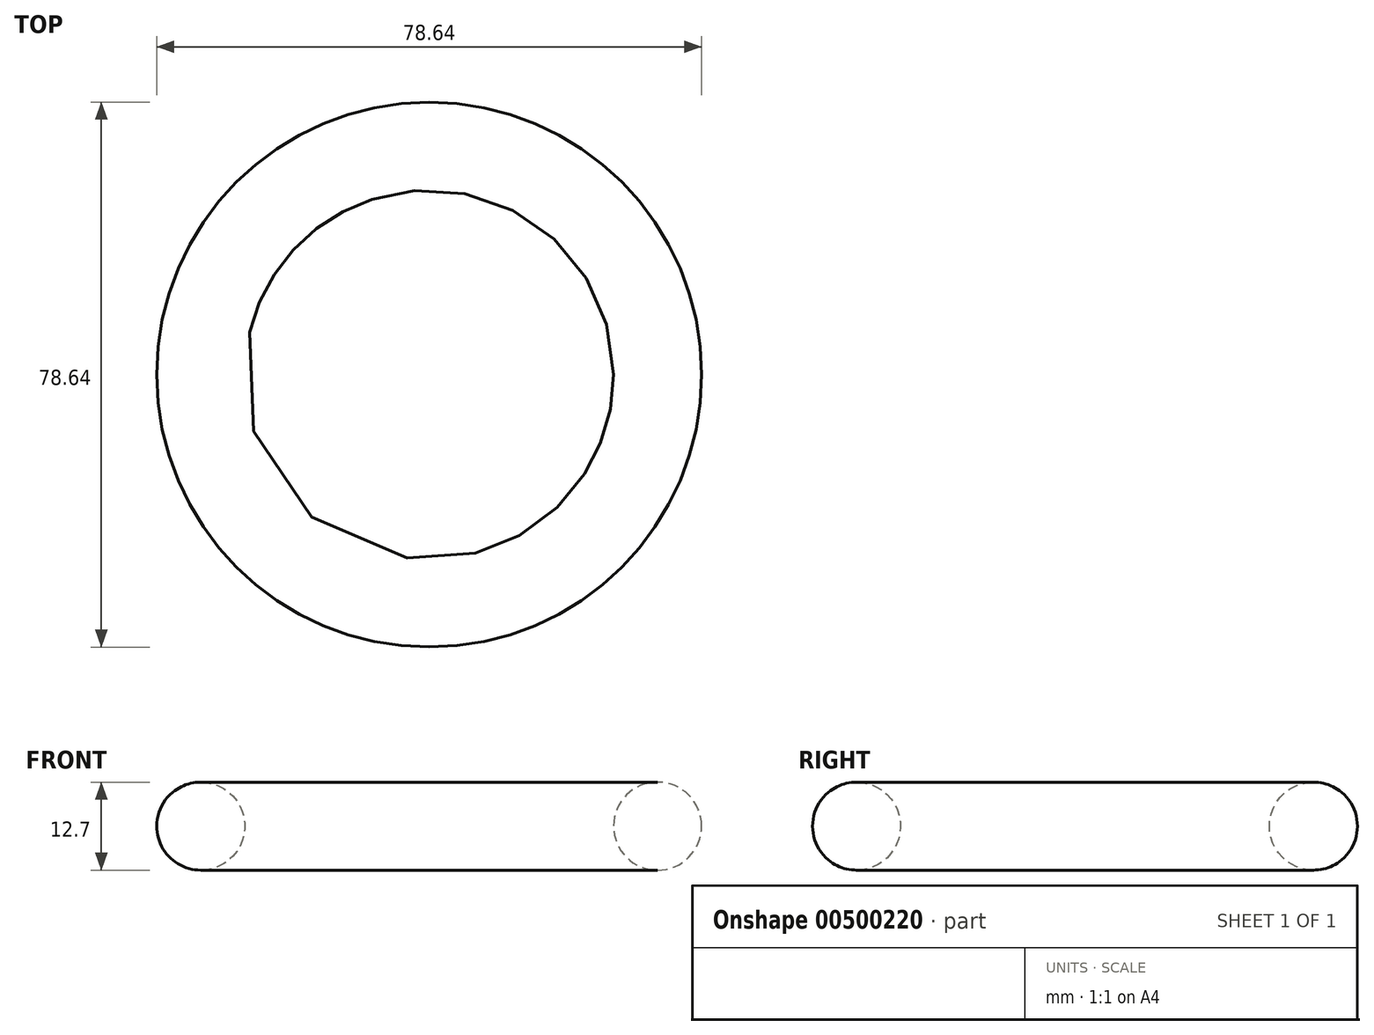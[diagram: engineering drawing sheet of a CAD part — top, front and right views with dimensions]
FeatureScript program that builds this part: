
annotation { "Feature Type Name" : "Feature", "Feature Type Description" : "" }
export const myFeature = defineFeature(function(context is Context, id is Id, definition is map)
    precondition{}
    {
        {
            var Q0;
            Q0=qCreatedBy(makeId("Top.planeOp"),FACE);
            var sketch = newSketch(context, id + "F0", { "sketchPlane" : qUnion([Q0])});
            skCircle(sketch, "E0", {"center": v(0, 0) * mm, "radius": 31.75 * mm});
            skSolve(sketch);
        }
        {
            var Q0;
            Q0=qCreatedBy(makeId("Front.planeOp"),FACE);
            var sketch = newSketch(context, id + "F1", { "sketchPlane" : qUnion([Q0])});
            skCircle(sketch, "E1", {"center": v(-32.97, 0) * mm, "radius": 6.35 * mm});
            skSolve(sketch);
        }
        {
            var Q0;
            Q0=makeQuery(id+"F1.imprint","IMPRINT",FACE,{"disambiguationData":[TD([[makeQuery(id+"F1.imprint","IMPRINT",EDGE,{"derivedFrom":sQuery(id+"F1.wireOp",EDGE,"E1")}),1.0]])]});
            var Q1;
            Q1=sQuery(id+"F0.wireOp",EDGE,"E0");
            sweep(context, id + "F2", {"profiles" : qUnion([Q0]), "path" : qUnion([Q1])});
        }
    });
